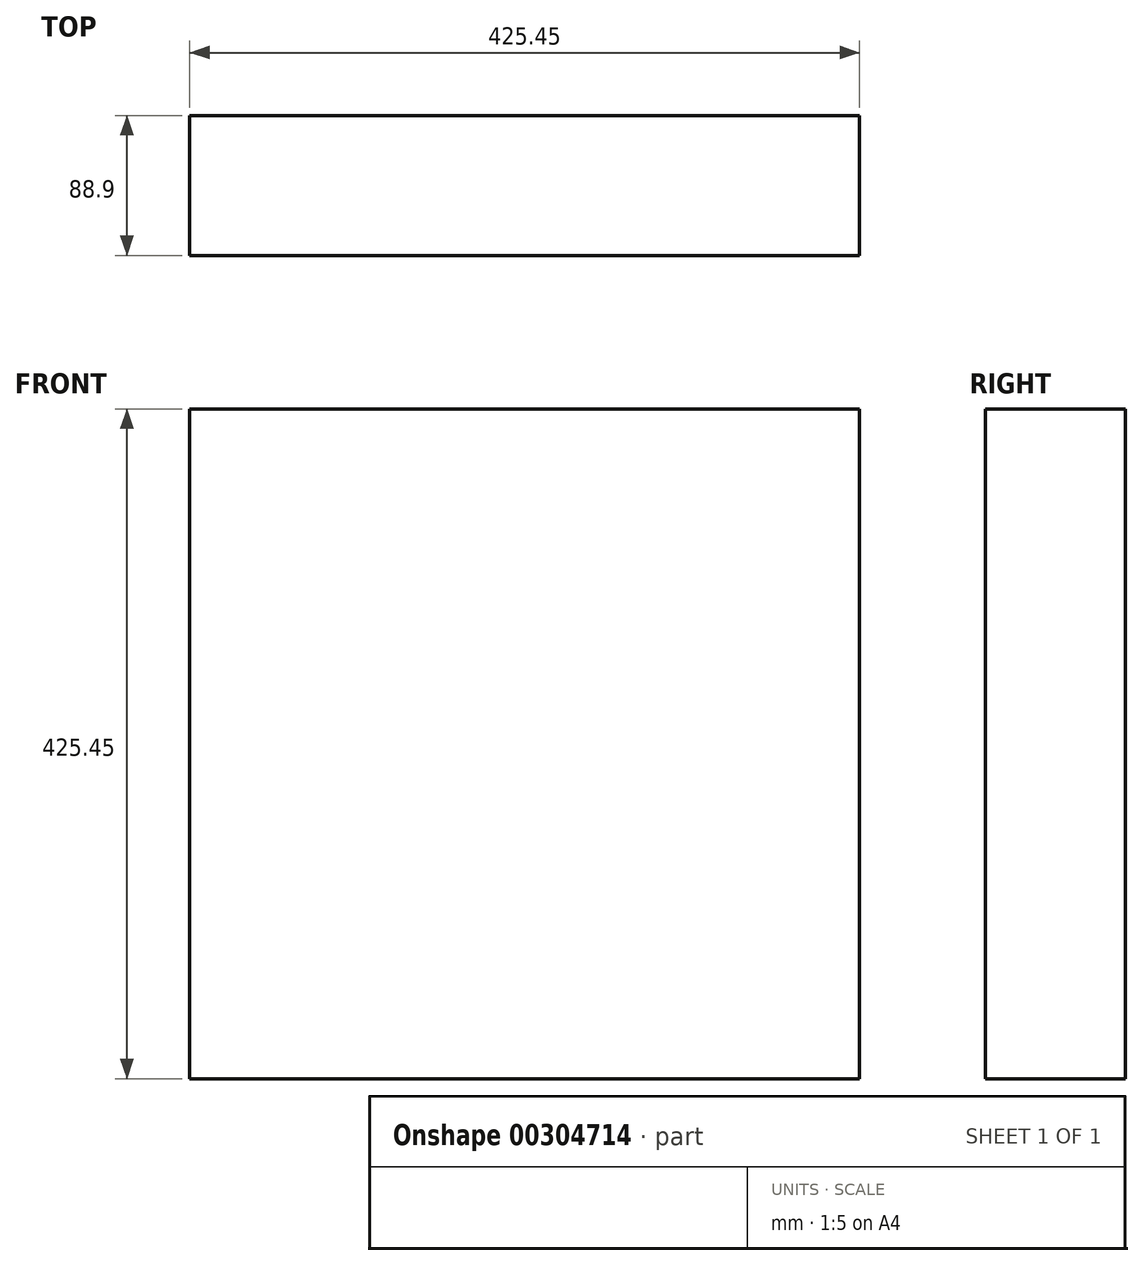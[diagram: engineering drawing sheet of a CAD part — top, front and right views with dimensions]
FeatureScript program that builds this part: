
annotation { "Feature Type Name" : "Feature", "Feature Type Description" : "" }
export const myFeature = defineFeature(function(context is Context, id is Id, definition is map)
    precondition{}
    {
        {
            var Q0;
            Q0=qCreatedBy(makeId("Front.planeOp"),FACE);
            var sketch = newSketch(context, id + "F0", { "sketchPlane" : qUnion([Q0])});
            skLineSegment(sketch, "E0.bottom", {"start": v(-210.24, 24.24) * mm, "end": v(215.21, 24.24) * mm});
            skLineSegment(sketch, "E0.top", {"start": v(-210.24, -401.21) * mm, "end": v(215.21, -401.21) * mm});
            skLineSegment(sketch, "E0.left", {"start": v(-210.24, 24.24) * mm, "end": v(-210.24, -401.21) * mm});
            skLineSegment(sketch, "E0.right", {"start": v(215.21, 24.24) * mm, "end": v(215.21, -401.21) * mm});
            skSolve(sketch);
        }
        {
            var Q0;
            Q0=makeQuery(id+"F0.imprint","IMPRINT",FACE,{"disambiguationData":[TD([[makeQuery(id+"F0.imprint","IMPRINT",EDGE,{"derivedFrom":sQuery(id+"F0.wireOp",EDGE,"E0.bottom")}),-1.0]])]});
            extrude(context, id + "F1", {"entities" : qUnion([Q0]), "depth" : 88.9 * mm});
        }
    });
